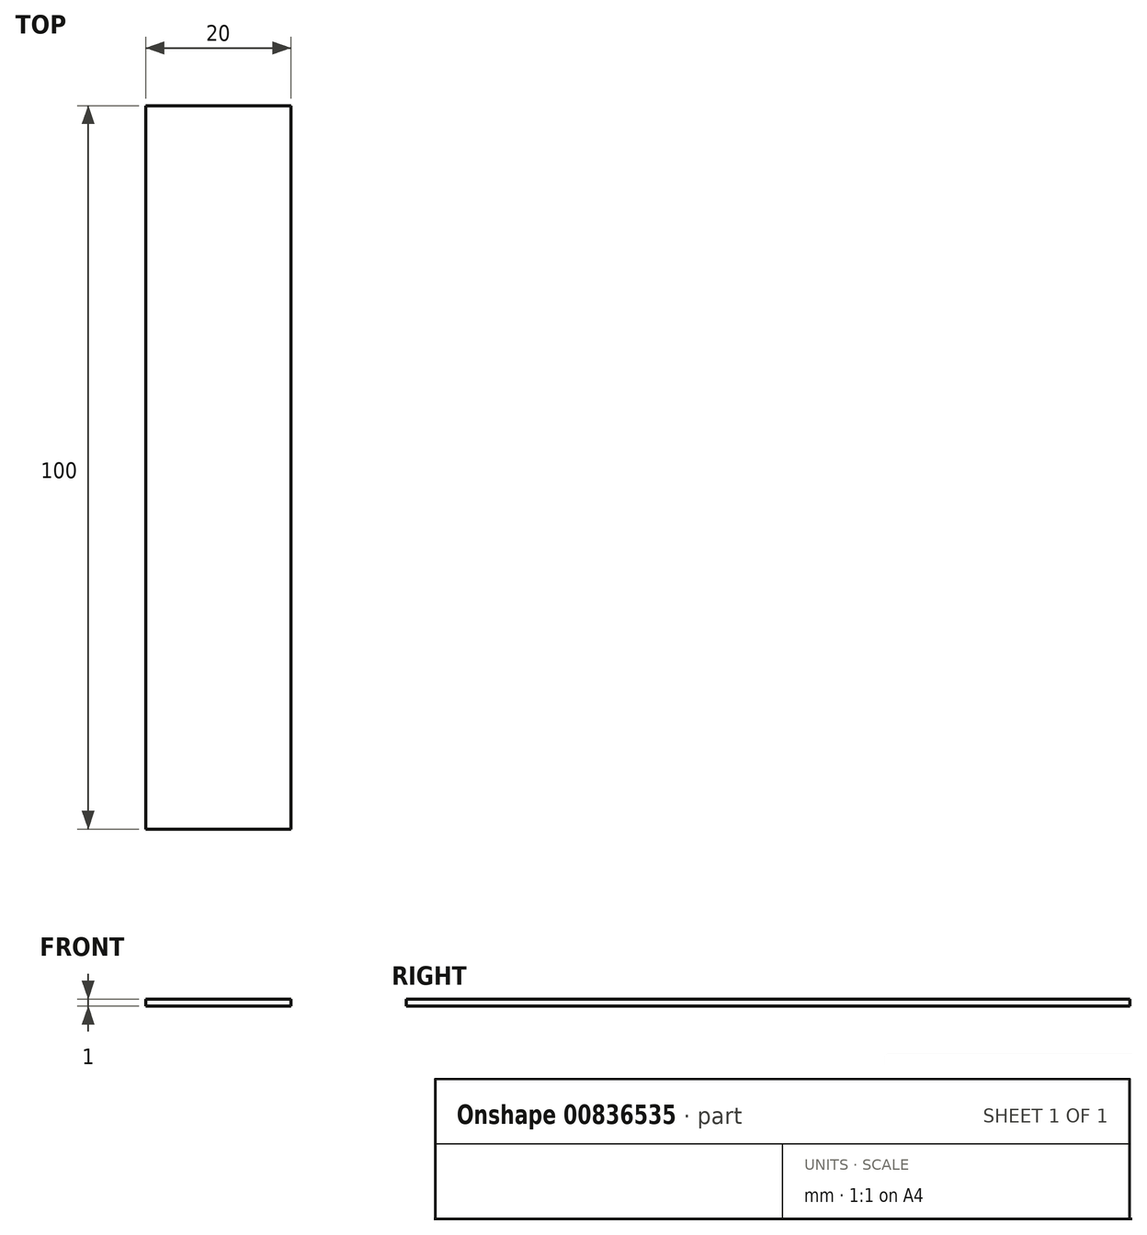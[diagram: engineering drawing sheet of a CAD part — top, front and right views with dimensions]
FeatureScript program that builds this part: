
annotation { "Feature Type Name" : "Feature", "Feature Type Description" : "" }
export const myFeature = defineFeature(function(context is Context, id is Id, definition is map)
    precondition{}
    {
        {
            var Q0;
            Q0=qCreatedBy(makeId("Top.planeOp"),FACE);
            var sketch = newSketch(context, id + "F0", { "sketchPlane" : qUnion([Q0])});
            skLineSegment(sketch, "E0.bottom", {"start": v(0, 0) * mm, "end": v(20, 0) * mm});
            skLineSegment(sketch, "E0.top", {"start": v(0, -100) * mm, "end": v(20, -100) * mm});
            skLineSegment(sketch, "E0.left", {"start": v(0, 0) * mm, "end": v(0, -100) * mm});
            skLineSegment(sketch, "E0.right", {"start": v(20, 0) * mm, "end": v(20, -100) * mm});
            skSolve(sketch);
        }
        {
            var Q0;
            Q0=makeQuery(id+"F0.imprint","IMPRINT",FACE,{"disambiguationData":[TD([[makeQuery(id+"F0.imprint","IMPRINT",EDGE,{"derivedFrom":sQuery(id+"F0.wireOp",EDGE,"E0.bottom")}),-1.0]])]});
            extrude(context, id + "F1", {"entities" : qUnion([Q0]), "depth" : 1 * mm, "offsetDistance" : 25 * mm});
        }
    });
